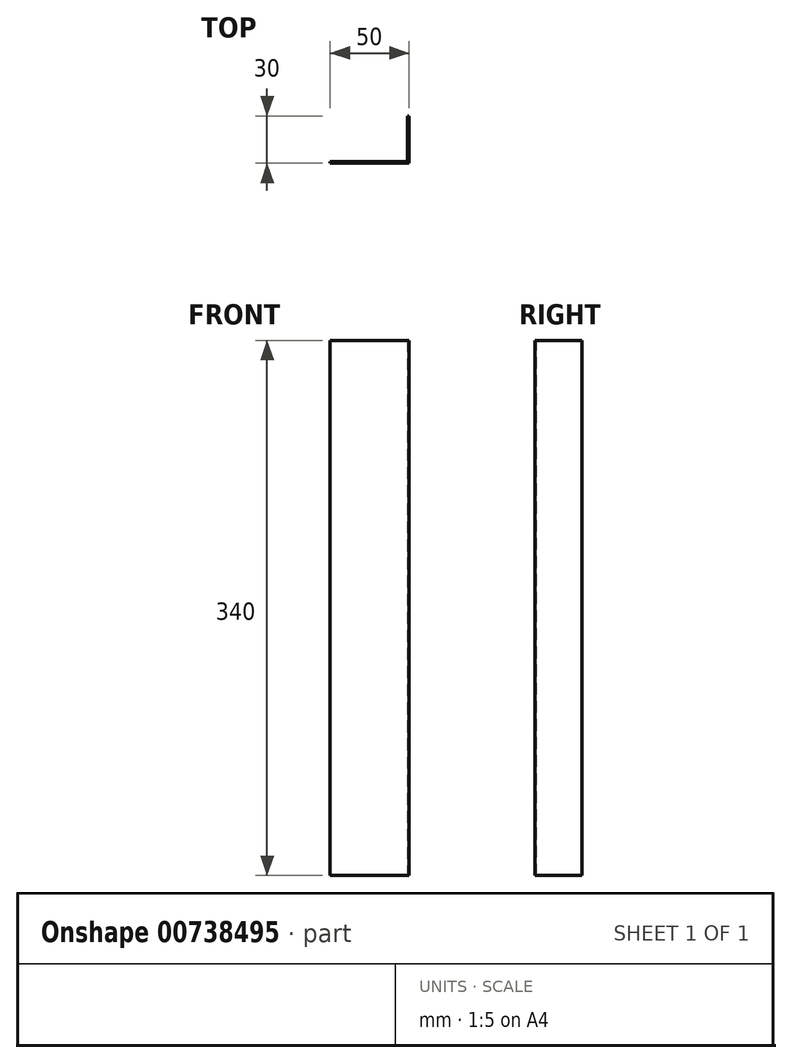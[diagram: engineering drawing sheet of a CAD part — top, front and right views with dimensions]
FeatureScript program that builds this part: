
annotation { "Feature Type Name" : "Feature", "Feature Type Description" : "" }
export const myFeature = defineFeature(function(context is Context, id is Id, definition is map)
    precondition{}
    {
        {
            var Q0;
            Q0=qCreatedBy(makeId("Front.planeOp"),FACE);
            var sketch = newSketch(context, id + "F0", { "sketchPlane" : qUnion([Q0])});
            skLineSegment(sketch, "E0.bottom", {"start": v(0, 0) * mm, "end": v(50, 0) * mm});
            skLineSegment(sketch, "E0.top", {"start": v(0, 340) * mm, "end": v(50, 340) * mm});
            skLineSegment(sketch, "E0.left", {"start": v(0, 0) * mm, "end": v(0, 340) * mm});
            skLineSegment(sketch, "E0.right", {"start": v(50, 0) * mm, "end": v(50, 340) * mm});
            skSolve(sketch);
        }
        {
            var Q0;
            Q0=makeQuery(id+"F0.imprint","IMPRINT",FACE,{"disambiguationData":[TD([[makeQuery(id+"F0.imprint","IMPRINT",EDGE,{"derivedFrom":sQuery(id+"F0.wireOp",EDGE,"E0.bottom")}),1.0]])]});
            extrude(context, id + "F1", {"entities" : qUnion([Q0]), "depth" : 1 * mm, "offsetDistance" : 25 * mm});
        }
        {
            var Q0;
            Q0=makeQuery(id+"F1.opExtrude","CAP_FACE",FACE,{"disambiguationData":[OSD([sQuery(id+"F0.wireOp",EDGE,"E0.bottom"),sQuery(id+"F0.wireOp",EDGE,"E0.top"),sQuery(id+"F0.wireOp",EDGE,"E0.left"),sQuery(id+"F0.wireOp",EDGE,"E0.right")])],"isStart":true});
            var sketch = newSketch(context, id + "F2", { "sketchPlane" : qUnion([Q0])});
            skLineSegment(sketch, "E1.bottom", {"start": v(-50, 340) * mm, "end": v(-49, 340) * mm});
            skLineSegment(sketch, "E1.top", {"start": v(-50, 0) * mm, "end": v(-49, 0) * mm});
            skLineSegment(sketch, "E1.left", {"start": v(-50, 340) * mm, "end": v(-50, 0) * mm});
            skLineSegment(sketch, "E1.right", {"start": v(-49, 340) * mm, "end": v(-49, 0) * mm});
            skSolve(sketch);
        }
        {
            var Q0;
            Q0 = qSketchRegion(id + "F2", true);
            extrude(context, id + "F3", {"entities" : qUnion([Q0]), "operationType" : NewBodyOperationType.ADD, "depth" : 29 * mm, "offsetDistance" : 25 * mm});
        }
    });
